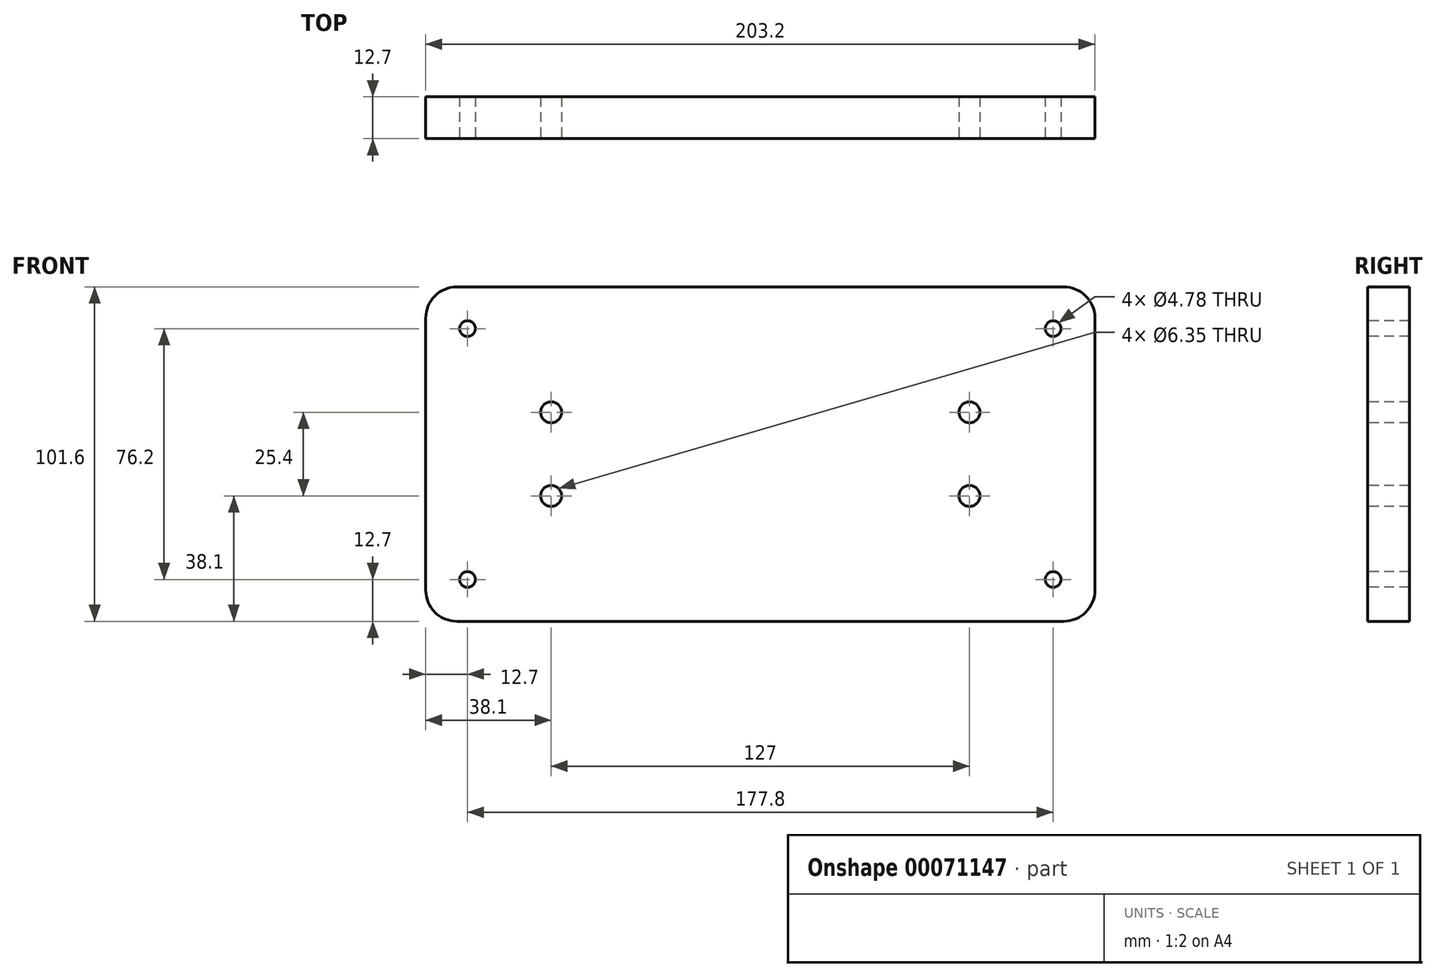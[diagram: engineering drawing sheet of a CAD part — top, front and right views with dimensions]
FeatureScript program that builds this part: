
annotation { "Feature Type Name" : "Feature", "Feature Type Description" : "" }
export const myFeature = defineFeature(function(context is Context, id is Id, definition is map)
    precondition{}
    {
        {
            var Q0;
            Q0=qCreatedBy(makeId("Front.planeOp"),FACE);
            var sketch = newSketch(context, id + "F0", { "sketchPlane" : qUnion([Q0])});
            skLineSegment(sketch, "E0.bottom", {"start": v(0, 0) * mm, "end": v(203.2, 0) * mm});
            skLineSegment(sketch, "E0.top", {"start": v(0, 101.6) * mm, "end": v(203.2, 101.6) * mm});
            skLineSegment(sketch, "E0.left", {"start": v(0, 0) * mm, "end": v(0, 101.6) * mm});
            skLineSegment(sketch, "E0.right", {"start": v(203.2, 0) * mm, "end": v(203.2, 101.6) * mm});
            skSolve(sketch);
        }
        {
            var Q0;
            Q0=makeQuery(id+"F0.imprint","IMPRINT",FACE,{"disambiguationData":[TD([[makeQuery(id+"F0.imprint","IMPRINT",EDGE,{"derivedFrom":sQuery(id+"F0.wireOp",EDGE,"E0.bottom")}),1.0]])]});
            extrude(context, id + "F1", {"entities" : qUnion([Q0]), "depth" : 12.7 * mm});
        }
        {
            var Q0;
            Q0=makeQuery(id+"F1.opExtrude","SWEPT_EDGE",EDGE,{"disambiguationData":[OSD([sQuery(id+"F0.wireOp",EDGE,"E0.top"),sQuery(id+"F0.wireOp",EDGE,"E0.left")])]});
            var Q1;
            Q1=makeQuery(id+"F1.opExtrude","SWEPT_EDGE",EDGE,{"disambiguationData":[OSD([sQuery(id+"F0.wireOp",EDGE,"E0.bottom"),sQuery(id+"F0.wireOp",EDGE,"E0.left")])]});
            var Q2;
            Q2=makeQuery(id+"F1.opExtrude","SWEPT_EDGE",EDGE,{"disambiguationData":[OSD([sQuery(id+"F0.wireOp",EDGE,"E0.bottom"),sQuery(id+"F0.wireOp",EDGE,"E0.right")])]});
            var Q3;
            Q3=makeQuery(id+"F1.opExtrude","SWEPT_EDGE",EDGE,{"disambiguationData":[OSD([sQuery(id+"F0.wireOp",EDGE,"E0.top"),sQuery(id+"F0.wireOp",EDGE,"E0.right")])]});
            fillet(context, id + "F2", {"entities" : qUnion([Q0, Q1, Q2, Q3]), "radius" : 9.52 * mm, "tangentPropagation" : true, "allowEdgeOverflow" : false});
        }
        {
            var Q0;
            Q0=makeQuery(id+"F1.opExtrude","CAP_FACE",FACE,{"disambiguationData":[OSD([sQuery(id+"F0.wireOp",EDGE,"E0.bottom"),sQuery(id+"F0.wireOp",EDGE,"E0.top"),sQuery(id+"F0.wireOp",EDGE,"E0.left"),sQuery(id+"F0.wireOp",EDGE,"E0.right")])],"isStart":false});
            var sketch = newSketch(context, id + "F3", { "sketchPlane" : qUnion([Q0])});
            skPoint(sketch, "E1", {"position": v(12.7, 12.7) * mm});
            skPoint(sketch, "E2", {"position": v(190.5, 12.7) * mm});
            skPoint(sketch, "E3", {"position": v(12.7, 88.9) * mm});
            skPoint(sketch, "E4", {"position": v(190.5, 88.9) * mm});
            skSolve(sketch);
        }
        {
            var Q0;
            Q0=sQuery(id+"F3.wireOp",VERTEX,"E3");
            var Q1;
            Q1=sQuery(id+"F3.wireOp",VERTEX,"E1");
            var Q2;
            Q2=sQuery(id+"F3.wireOp",VERTEX,"E2");
            var Q3;
            Q3=sQuery(id+"F3.wireOp",VERTEX,"E4");
            var Q4;
            Q4=makeQuery(id+"F1.opExtrude","SWEPT_BODY",BODY,{"disambiguationData":[OSD([sQuery(id+"F0.wireOp",EDGE,"E0.bottom"),sQuery(id+"F0.wireOp",EDGE,"E0.top"),sQuery(id+"F0.wireOp",EDGE,"E0.left"),sQuery(id+"F0.wireOp",EDGE,"E0.right")])]});
            hole(context, id + "F4", {"style" : HoleStyle.SIMPLE, "holeDiameter" : 4.78 * mm, "endStyle" : HoleEndStyle.THROUGH, "locations" : qUnion([Q0, Q1, Q2, Q3]), "scope" : qUnion([Q4])});
        }
        {
            var Q0;
            Q0=makeQuery(id+"F1.opExtrude","CAP_FACE",FACE,{"disambiguationData":[OSD([sQuery(id+"F0.wireOp",EDGE,"E0.bottom"),sQuery(id+"F0.wireOp",EDGE,"E0.top"),sQuery(id+"F0.wireOp",EDGE,"E0.left"),sQuery(id+"F0.wireOp",EDGE,"E0.right")])],"isStart":false});
            var sketch = newSketch(context, id + "F5", { "sketchPlane" : qUnion([Q0])});
            skPoint(sketch, "E5", {"position": v(38.1, 63.5) * mm});
            skPoint(sketch, "E6", {"position": v(38.1, 38.1) * mm});
            skPoint(sketch, "E7", {"position": v(165.1, 63.5) * mm});
            skPoint(sketch, "E8", {"position": v(165.1, 38.1) * mm});
            skSolve(sketch);
        }
        {
            var Q0;
            Q0=sQuery(id+"F5.wireOp",VERTEX,"E5");
            var Q1;
            Q1=sQuery(id+"F5.wireOp",VERTEX,"E6");
            var Q2;
            Q2=sQuery(id+"F5.wireOp",VERTEX,"E7");
            var Q3;
            Q3=sQuery(id+"F5.wireOp",VERTEX,"E8");
            var Q4;
            Q4=makeQuery(id+"F1.opExtrude","SWEPT_BODY",BODY,{"disambiguationData":[OSD([sQuery(id+"F0.wireOp",EDGE,"E0.bottom"),sQuery(id+"F0.wireOp",EDGE,"E0.top"),sQuery(id+"F0.wireOp",EDGE,"E0.left"),sQuery(id+"F0.wireOp",EDGE,"E0.right")])]});
            hole(context, id + "F6", {"style" : HoleStyle.SIMPLE, "holeDiameter" : 6.35 * mm, "endStyle" : HoleEndStyle.THROUGH, "locations" : qUnion([Q0, Q1, Q2, Q3]), "scope" : qUnion([Q4])});
        }
    });
